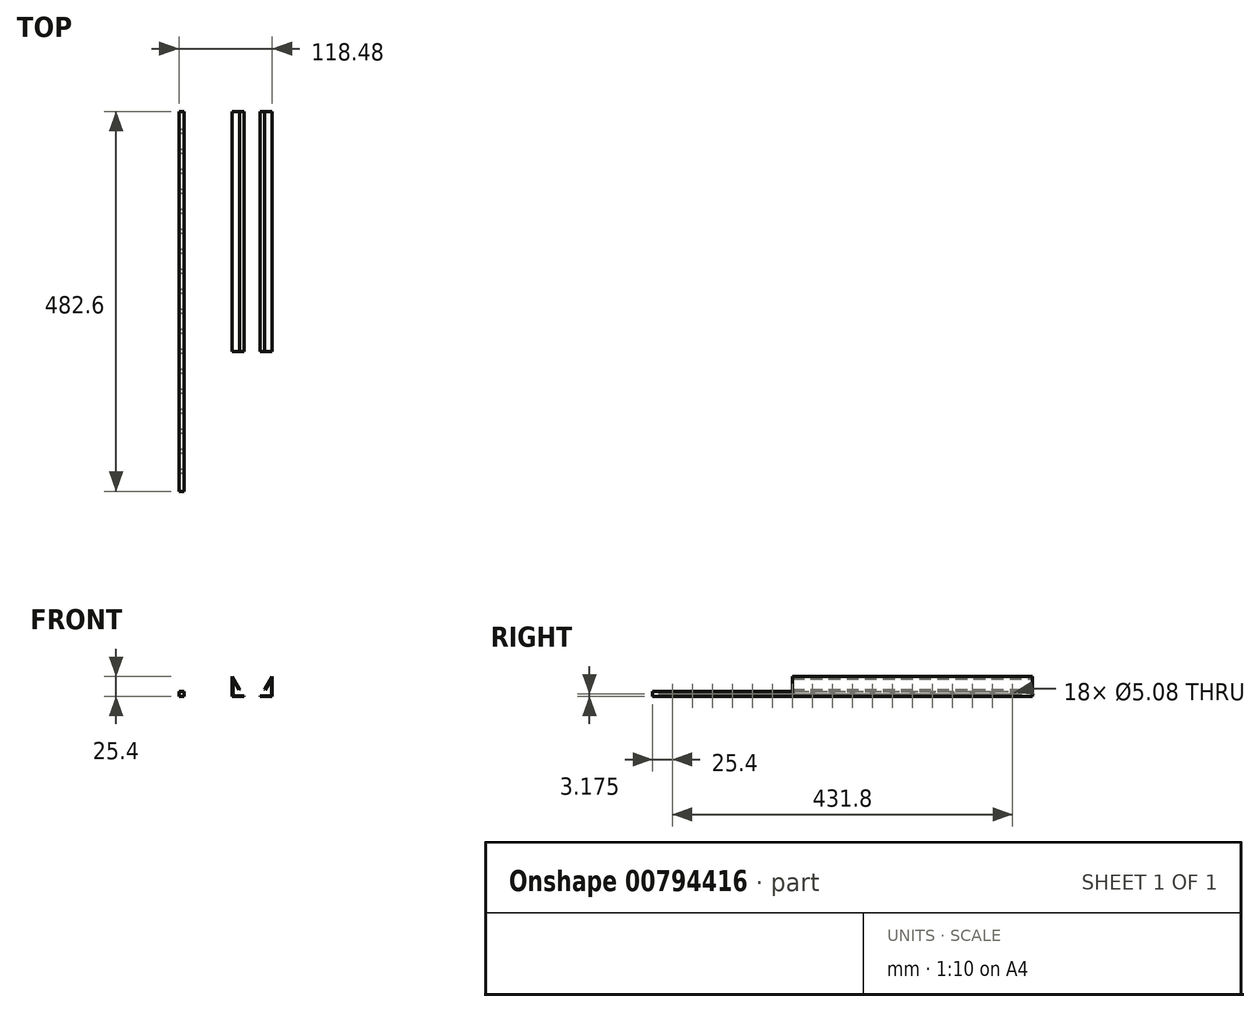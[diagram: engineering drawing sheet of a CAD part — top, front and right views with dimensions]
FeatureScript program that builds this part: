
annotation { "Feature Type Name" : "Feature", "Feature Type Description" : "" }
export const myFeature = defineFeature(function(context is Context, id is Id, definition is map)
    precondition{}
    {
        {
            var Q0;
            Q0=qCreatedBy(makeId("Front.planeOp"),FACE);
            var sketch = newSketch(context, id + "F0", { "sketchPlane" : qUnion([Q0])});
            skLineSegment(sketch, "E0", {"start": v(0, 0) * mm, "end": v(0, 25.4) * mm});
            skLineSegment(sketch, "E1", {"start": v(0, 0) * mm, "end": v(15.24, 0) * mm});
            skLineSegment(sketch, "E2", {"start": v(15.24, 0) * mm, "end": v(15.24, 0.89) * mm});
            skLineSegment(sketch, "E3", {"start": v(15.24, 0.89) * mm, "end": v(0.89, 0.89) * mm});
            skLineSegment(sketch, "E4", {"start": v(0, 25.4) * mm, "end": v(9.52, 8.9) * mm});
            skLineSegment(sketch, "E5", {"start": v(0.89, 0.89) * mm, "end": v(0.89, 22.2) * mm});
            skLineSegment(sketch, "E6", {"start": v(0.89, 22.2) * mm, "end": v(8.97, 8.2) * mm});
            skLineSegment(sketch, "E7", {"start": v(8.97, 8.2) * mm, "end": v(9.52, 8.9) * mm});
            skSolve(sketch);
        }
        {
            var Q0;
            Q0 = qSketchRegion(id + "F0", true);
            extrude(context, id + "F1", {"entities" : qUnion([Q0]), "depth" : 304.8 * mm, "offsetDistance" : 25.4 * mm});
        }
        {
            var Q0;
            Q0=qCreatedBy(makeId("Front.planeOp"),FACE);
            var sketch = newSketch(context, id + "F2", { "sketchPlane" : qUnion([Q0])});
            skLineSegment(sketch, "E8", {"start": v(-67.68, 0) * mm, "end": v(-67.68, 6.35) * mm});
            skLineSegment(sketch, "E9", {"start": v(-67.68, 6.35) * mm, "end": v(-61.33, 6.35) * mm});
            skLineSegment(sketch, "E10", {"start": v(-61.33, 6.35) * mm, "end": v(-61.33, 0) * mm});
            skLineSegment(sketch, "E11", {"start": v(-61.33, 0) * mm, "end": v(-67.68, 0) * mm});
            skSolve(sketch);
        }
        {
            var Q0;
            Q0 = qSketchRegion(id + "F2", true);
            extrude(context, id + "F3", {"entities" : qUnion([Q0]), "depth" : 482.6 * mm, "offsetDistance" : 25.4 * mm});
        }
        {
            var Q0;
            Q0=makeQuery(id+"F3.opExtrude","SWEPT_FACE",FACE,{"disambiguationData":[OSD([sQuery(id+"F2.wireOp",EDGE,"E8")])]});
            var sketch = newSketch(context, id + "F4", { "sketchPlane" : qUnion([Q0])});
            skCircle(sketch, "E12", {"center": v(25.4, 3.18) * mm, "radius": 2.54 * mm});
            skCircle(sketch, "E13.1.0.0", {"center": v(50.8, 3.18) * mm, "radius": 2.54 * mm});
            skCircle(sketch, "E13.2.0.0", {"center": v(76.2, 3.18) * mm, "radius": 2.54 * mm});
            skCircle(sketch, "E13.3.0.0", {"center": v(101.6, 3.18) * mm, "radius": 2.54 * mm});
            skCircle(sketch, "E13.4.0.0", {"center": v(127, 3.18) * mm, "radius": 2.54 * mm});
            skCircle(sketch, "E13.5.0.0", {"center": v(152.4, 3.18) * mm, "radius": 2.54 * mm});
            skCircle(sketch, "E13.6.0.0", {"center": v(177.8, 3.18) * mm, "radius": 2.54 * mm});
            skCircle(sketch, "E13.7.0.0", {"center": v(203.2, 3.18) * mm, "radius": 2.54 * mm});
            skCircle(sketch, "E13.8.0.0", {"center": v(228.6, 3.18) * mm, "radius": 2.54 * mm});
            skCircle(sketch, "E13.9.0.0", {"center": v(254, 3.18) * mm, "radius": 2.54 * mm});
            skCircle(sketch, "E13.10.0.0", {"center": v(279.4, 3.18) * mm, "radius": 2.54 * mm});
            skCircle(sketch, "E13.11.0.0", {"center": v(304.8, 3.18) * mm, "radius": 2.54 * mm});
            skCircle(sketch, "E13.12.0.0", {"center": v(330.2, 3.18) * mm, "radius": 2.54 * mm});
            skCircle(sketch, "E13.13.0.0", {"center": v(355.6, 3.18) * mm, "radius": 2.54 * mm});
            skCircle(sketch, "E13.14.0.0", {"center": v(381, 3.18) * mm, "radius": 2.54 * mm});
            skCircle(sketch, "E13.15.0.0", {"center": v(406.4, 3.18) * mm, "radius": 2.54 * mm});
            skCircle(sketch, "E13.16.0.0", {"center": v(431.8, 3.18) * mm, "radius": 2.54 * mm});
            skLineSegment(sketch, "E13.direction1", {"start": v(25.4, 3.18) * mm, "end": v(50.8, 3.18) * mm, "construction": true});
            skCircle(sketch, "E14.0.17.0", {"center": v(457.2, 3.18) * mm, "radius": 2.54 * mm});
            skSolve(sketch);
        }
        {
            var Q0;
            Q0 = qSketchRegion(id + "F4", true);
            extrude(context, id + "F5", {"entities" : qUnion([Q0]), "operationType" : NewBodyOperationType.REMOVE, "oppositeDirection" : true, "depth" : 6.35 * mm, "offsetDistance" : 25.4 * mm});
        }
        {
            var Q0;
            Q0=qCreatedBy(makeId("Right.planeOp"),FACE);
            cPlane(context, id + "F6", {"entities" : qUnion([Q0]), "cplaneType" : CPlaneType.OFFSET, "offset" : 25.4 * mm, "width" : 152.4 * mm, "height" : 152.4 * mm});
        }
        {
            var Q0;
            Q0=makeQuery(id+"F1.opExtrude","SWEPT_BODY",BODY,{"disambiguationData":[OSD([sQuery(id+"F0.wireOp",EDGE,"E0"),sQuery(id+"F0.wireOp",EDGE,"E1"),sQuery(id+"F0.wireOp",EDGE,"E2"),sQuery(id+"F0.wireOp",EDGE,"E3"),sQuery(id+"F0.wireOp",EDGE,"E4"),sQuery(id+"F0.wireOp",EDGE,"E5"),sQuery(id+"F0.wireOp",EDGE,"E6"),sQuery(id+"F0.wireOp",EDGE,"E7")])]});
            var Q1;
            Q1=qCreatedBy(id+"F6.planeOp",FACE);
            mirror(context, id + "F7", {"entities" : qUnion([Q0]), "mirrorPlane" : qUnion([Q1])});
        }
    });
